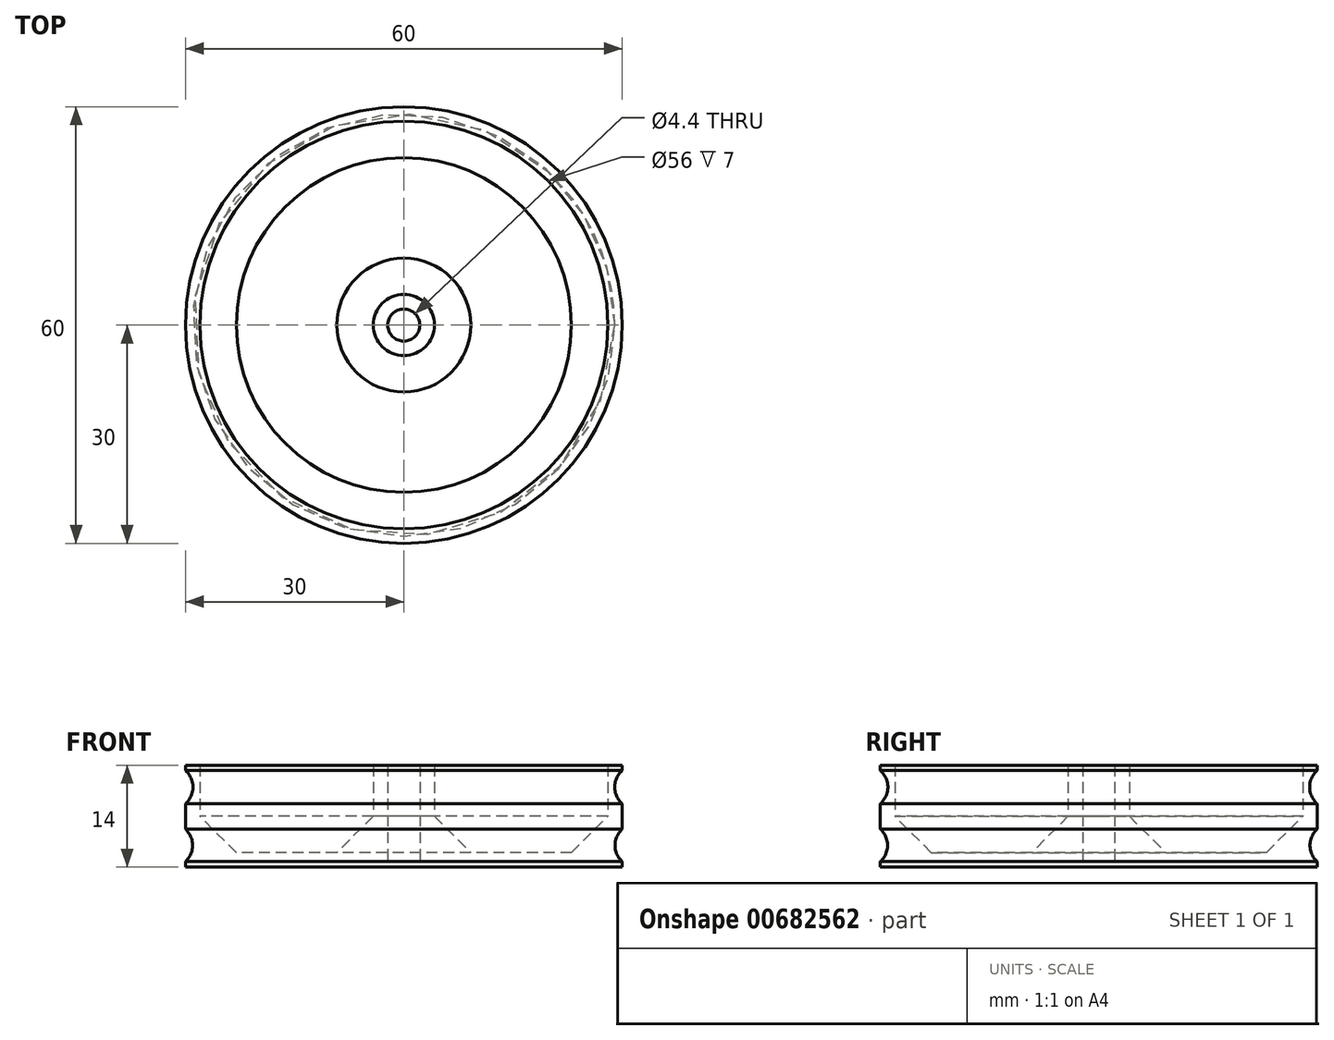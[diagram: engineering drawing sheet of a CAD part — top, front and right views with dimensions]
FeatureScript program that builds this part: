
annotation { "Feature Type Name" : "Feature", "Feature Type Description" : "" }
export const myFeature = defineFeature(function(context is Context, id is Id, definition is map)
    precondition{}
    {
        {
            var Q0;
            Q0=qCreatedBy(makeId("Top.planeOp"),FACE);
            var sketch = newSketch(context, id + "F0", { "sketchPlane" : qUnion([Q0])});
            skCircle(sketch, "E0", {"center": v(0, 0) * mm, "radius": 30 * mm});
            skCircle(sketch, "E1", {"center": v(0, 0) * mm, "radius": 2.2 * mm});
            skSolve(sketch);
        }
        {
            var Q0;
            Q0=makeQuery(id+"F0.imprint","IMPRINT",FACE,{"disambiguationData":[TD([[makeQuery(id+"F0.imprint","IMPRINT",EDGE,{"derivedFrom":sQuery(id+"F0.wireOp",EDGE,"E0")}),1.0]])]});
            extrude(context, id + "F1", {"entities" : qUnion([Q0]), "depth" : 14 * mm, "offsetDistance" : 25 * mm});
        }
        {
            var Q0;
            Q0=makeQuery(id+"F1.opExtrude","CAP_FACE",FACE,{"disambiguationData":[OSD([sQuery(id+"F0.wireOp",EDGE,"E0"),sQuery(id+"F0.wireOp",EDGE,"E1")])],"isStart":false});
            shell(context, id + "F2", {"entities" : qUnion([Q0]), "thickness" : 2 * mm});
        }
        {
            var Q0;
            {var subQ0=sQuery(id+"F0.wireOp",EDGE,"E0");Q0=makeQuery(id+"F2.opShell","OFFSET_EDGE",EDGE,{"disambiguationData":[OSD([subQ0]),TDD([makeQuery(id+"F1.opExtrude","CAP_EDGE",EDGE,{"disambiguationData":[OSD([subQ0])],"isStart":true})])]});}
            var Q1;
            {var subQ0=sQuery(id+"F0.wireOp",EDGE,"E1");Q1=makeQuery(id+"F2.opShell","OFFSET_EDGE",EDGE,{"disambiguationData":[OSD([subQ0]),TDD([makeQuery(id+"F1.opExtrude","CAP_EDGE",EDGE,{"disambiguationData":[OSD([subQ0])],"isStart":true})])]});}
            chamfer(context, id + "F3", {"entities" : qUnion([Q0, Q1]), "width" : 5 * mm, "tangentPropagation" : true});
        }
        {
            var Q0;
            Q0=qCreatedBy(makeId("Front.planeOp"),FACE);
            var sketch = newSketch(context, id + "F4", { "sketchPlane" : qUnion([Q0])});
            skCircle(sketch, "E2", {"center": v(-31.95, 11) * mm, "radius": 3 * mm});
            skCircle(sketch, "E3", {"center": v(-32, 3) * mm, "radius": 3 * mm});
            skLineSegment(sketch, "E4", {"start": v(-32, 3) * mm, "end": v(-31.95, 11) * mm, "construction": true});
            skLineSegment(sketch, "E5", {"start": v(-31.95, 14) * mm, "end": v(-27.1, 14) * mm, "construction": true});
            skLineSegment(sketch, "E6", {"start": v(-32.03, 0) * mm, "end": v(-27.86, 0) * mm, "construction": true});
            skLineSegment(sketch, "E7", {"start": v(-31.98, 6) * mm, "end": v(-31.97, 8) * mm, "construction": true});
            skLineSegment(sketch, "E8", {"start": v(-31.97, 8) * mm, "end": v(-31.98, 6) * mm, "construction": true});
            skSolve(sketch);
        }
        {
            var Q0;
            Q0=makeQuery(id+"F4.imprint","IMPRINT",FACE,{"disambiguationData":[TD([[makeQuery(id+"F4.imprint","IMPRINT",EDGE,{"derivedFrom":sQuery(id+"F4.wireOp",EDGE,"E3")}),1.0]])]});
            var Q1;
            Q1=makeQuery(id+"F4.imprint","IMPRINT",FACE,{"disambiguationData":[TD([[makeQuery(id+"F4.imprint","IMPRINT",EDGE,{"derivedFrom":sQuery(id+"F4.wireOp",EDGE,"E2")}),1.0]])]});
            var Q2;
            Q2=makeQuery(id+"F1.opExtrude","CAP_EDGE",EDGE,{"disambiguationData":[OSD([sQuery(id+"F0.wireOp",EDGE,"E0")])],"isStart":false});
            sweep(context, id + "F5", {"operationType" : NewBodyOperationType.REMOVE, "profiles" : qUnion([Q0, Q1]), "path" : qUnion([Q2])});
        }
    });
